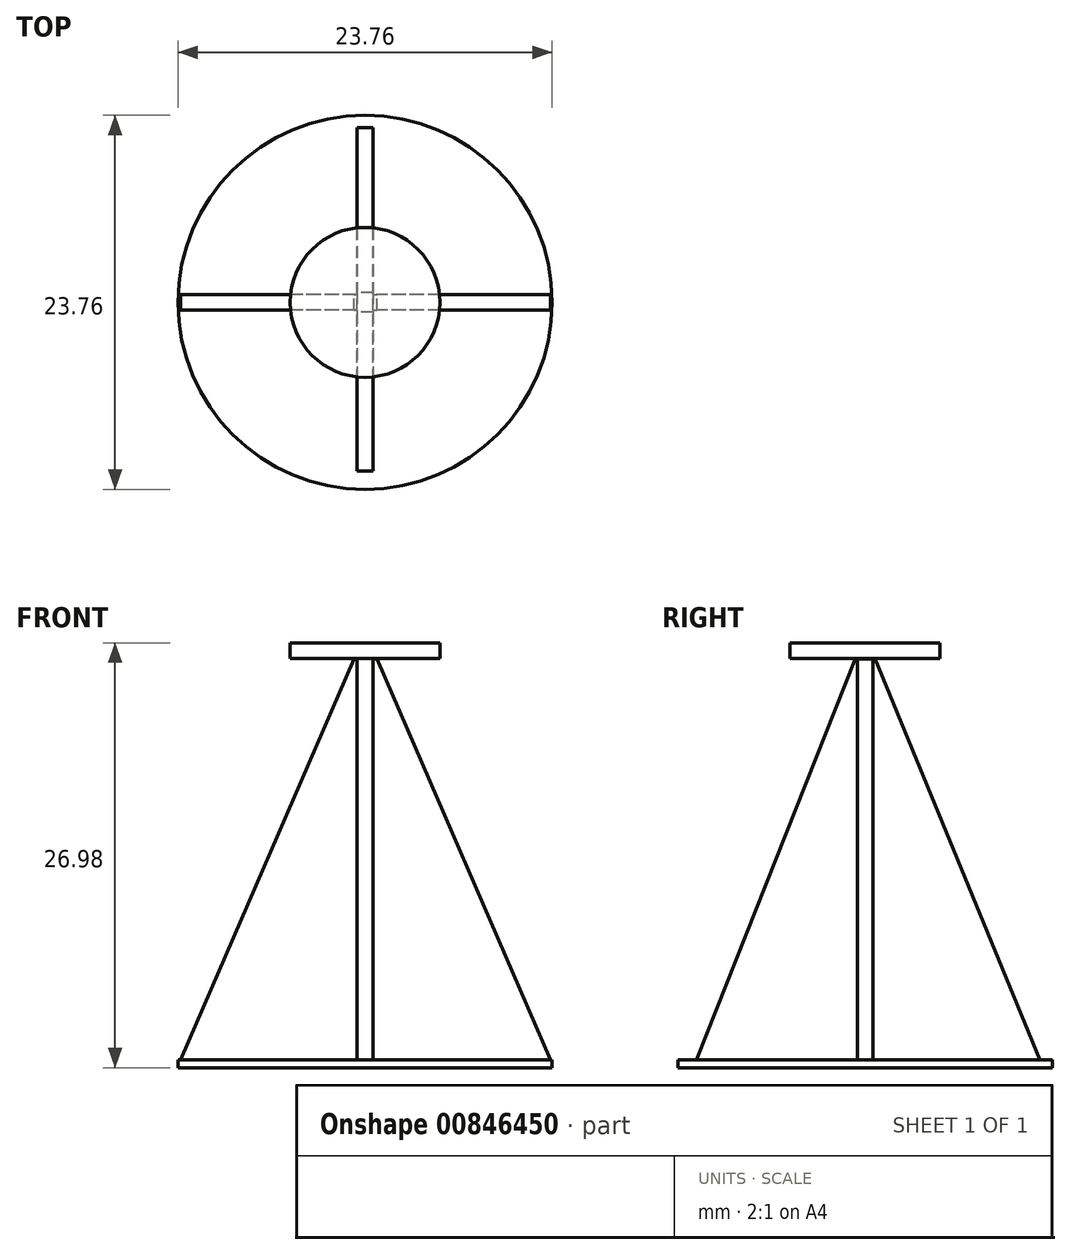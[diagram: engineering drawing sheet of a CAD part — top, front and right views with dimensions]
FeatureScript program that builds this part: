
annotation { "Feature Type Name" : "Feature", "Feature Type Description" : "" }
export const myFeature = defineFeature(function(context is Context, id is Id, definition is map)
    precondition{}
    {
        {
            var Q0;
            Q0=qCreatedBy(makeId("Front.planeOp"),FACE);
            var sketch = newSketch(context, id + "F0", { "sketchPlane" : qUnion([Q0])});
            skLineSegment(sketch, "E0", {"start": v(-0.69, 25.46) * mm, "end": v(-11.72, 0) * mm});
            skLineSegment(sketch, "E1", {"start": v(-0.69, 25.46) * mm, "end": v(0.77, 25.46) * mm});
            skPoint(sketch, "E2.orphan", {"position": v(0, 27.04) * mm});
            skLineSegment(sketch, "E3", {"start": v(11.8, 0) * mm, "end": v(-11.72, 0) * mm});
            skPoint(sketch, "E4.orphan", {"position": v(13.17, 0) * mm});
            skLineSegment(sketch, "E5", {"start": v(11.8, 0) * mm, "end": v(0.77, 25.46) * mm});
            skSolve(sketch);
        }
        {
            var Q0;
            Q0=qCreatedBy(makeId("Right.planeOp"),FACE);
            var sketch = newSketch(context, id + "F1", { "sketchPlane" : qUnion([Q0])});
            skLineSegment(sketch, "E6", {"start": v(-0.62, 25.48) * mm, "end": v(-10.73, 0) * mm});
            skLineSegment(sketch, "E7", {"start": v(-10.73, 0) * mm, "end": v(0, 0) * mm});
            skLineSegment(sketch, "E8", {"start": v(0, 0) * mm, "end": v(11.09, 0) * mm});
            skLineSegment(sketch, "E9", {"start": v(11.09, 0) * mm, "end": v(0.64, 25.48) * mm});
            skLineSegment(sketch, "E10", {"start": v(0, 25.48) * mm, "end": v(-0.62, 25.48) * mm});
            skLineSegment(sketch, "E11", {"start": v(-0.62, 25.48) * mm, "end": v(0, 25.48) * mm});
            skLineSegment(sketch, "E12", {"start": v(0, 25.48) * mm, "end": v(0.64, 25.48) * mm});
            skPoint(sketch, "E13.orphan", {"position": v(0, 27.04) * mm});
            skSolve(sketch);
        }
        {
            var Q0;
            Q0=qCreatedBy(makeId("Top.planeOp"),FACE);
            var sketch = newSketch(context, id + "F2", { "sketchPlane" : qUnion([Q0])});
            skCircle(sketch, "E14", {"center": v(0, 0) * mm, "radius": 11.88 * mm});
            skSolve(sketch);
        }
        {
            var Q0;
            Q0 = qSketchRegion(id + "F0", true);
            extrude(context, id + "F3", {"entities" : qUnion([Q0]), "endBound" : BoundingType.SYMMETRIC, "depth" : 1 * mm, "offsetDistance" : 25 * mm});
        }
        {
            var Q0;
            Q0 = qSketchRegion(id + "F1", true);
            extrude(context, id + "F4", {"entities" : qUnion([Q0]), "operationType" : NewBodyOperationType.ADD, "endBound" : BoundingType.SYMMETRIC, "depth" : 1 * mm, "offsetDistance" : 25 * mm});
        }
        {
            var Q0;
            Q0 = qSketchRegion(id + "F2", true);
            extrude(context, id + "F5", {"entities" : qUnion([Q0]), "operationType" : NewBodyOperationType.ADD, "oppositeDirection" : true, "depth" : 0.5 * mm, "offsetDistance" : 25 * mm});
        }
        {
            var Q0;
            Q0=makeQuery(id+"F4.opExtrude","SWEPT_FACE",FACE,{"disambiguationData":[OSD([sQuery(id+"F1.wireOp",EDGE,"E11"),sQuery(id+"F1.wireOp",EDGE,"E12")])]});
            var sketch = newSketch(context, id + "F6", { "sketchPlane" : qUnion([Q0])});
            skCircle(sketch, "E15", {"center": v(0, 0) * mm, "radius": 4.76 * mm});
            skSolve(sketch);
        }
        {
            var Q0;
            Q0 = qSketchRegion(id + "F6", true);
            extrude(context, id + "F7", {"entities" : qUnion([Q0]), "operationType" : NewBodyOperationType.ADD, "depth" : 1 * mm, "offsetDistance" : 25 * mm});
        }
    });
